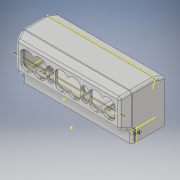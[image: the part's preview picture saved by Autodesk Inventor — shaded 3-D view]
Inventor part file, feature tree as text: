
AUTODESK INVENTOR PART (.ipt)
format: ipt  version: 2019 (Build 230136000, 136)  size: 1,148,416 bytes
history: native  units: mm
features: reference x93, sketch x32, extrude x29, plane x11, other x10, projected_geometry x10, mirror x6, hole x3, fillet x2, pattern_linear x1
ambient origin geometry x8: Origin, YZ Plane, XZ Plane, XY Plane, X Axis, Y Axis, Z Axis, Center Point
bodies: Body1 (feature_tree), Body2 (feature_tree), Body3 (feature_tree)
feature tree (197):
  other  "Querschnitt1"
  extrude  "Extrusion2"  Depth=4.0mm TaperAngle=0.0deg
  extrude  "Extrusion3"  TaperAngle=0.0deg  [1 undecoded]
  extrude  "Extrusion4"  Depth=4.0mm TaperAngle=0.0deg
  extrude  "Extrusion5"  Depth=4.0mm
  extrude  "Extrusion6"  Depth=0.5mm
  extrude  "Extrusion7"  Depth=0.5mm
  extrude  "Extrusion8"  Depth=4.0mm
  fillet  "Rundung1"  Radius=45.0mm
  extrude  "Extrusion9"  Depth=12.217305mm
  hole  "Bohrung1"  [1 undecoded]
  plane  "Arbeitsebene9"
  plane  "Arbeitsebene10"
  plane  "Arbeitsebene11"
  plane  "Arbeitsebene12"
  plane  "Arbeitsebene13"
  extrude  "Extrusion17"  Depth=30.0mm TaperAngle=0.0deg
  plane  "Arbeitsebene14"
  plane  "Arbeitsebene15"
  mirror  "Spiegeln4"
  extrude  "Extrusion18"  Depth=30.0mm TaperAngle=0.0deg
  extrude  "Extrusion19"  Depth=100.0mm
  extrude  "Extrusion20"  TaperAngle=0.0deg  [1 undecoded]
  mirror  "Spiegeln5"
  mirror  "Spiegeln6"
  mirror  "Spiegeln7"
  extrude  "Extrusion21"  Depth=4.0mm
  extrude  "Extrusion22"  Depth=20.0mm TaperAngle=0.0deg
  sketch  "Skizze31"  dims[d84=39.0mm d85=0.0mm d87=4.0mm]
  extrude  "Extrusion23"  Depth=15.0mm
  extrude  "Extrusion24"  Depth=100.0mm TaperAngle=0.0deg
  plane  "Arbeitsebene16"
  plane  "Arbeitsebene17"
  sketch  "Skizze34"  dims[d88=20.0mm d89=0.0mm d90=20.0mm d91=0.0mm]
  plane  "Arbeitsebene19"
  extrude  "Extrusion27"  Depth=1.0mm TaperAngle=0.0deg
  extrude  "Extrusion28"  Depth=0.14mm
  extrude  "Extrusion29"  Depth=1.0mm
  hole  "Bohrung2"  [1 undecoded]
  pattern_linear  "Rechteckige Anordnung1"  Count1=3 Spacing1=57.0mm
  extrude  "Extrusion30"  Depth=4.0mm TaperAngle=0.0deg
  plane  "Arbeitsebene20"
  extrude  "Extrusion34"  Depth=10.0mm
  extrude  "Extrusion35"  Depth=10.0mm TaperAngle=0.0deg
  extrude  "Extrusion36"  Depth=10.0mm
  extrude  "Extrusion37"  Depth=2.5mm
  extrude  "Extrusion38"  Depth=1.0mm
  extrude  "Extrusion39"  Depth=4.0mm TaperAngle=0.0deg
  extrude  "Extrusion40"  Depth=4.0mm
  extrude  "Extrusion41"  Depth=4.0mm
  mirror  "Spiegeln8"
  hole  "Bohrung3"  [1 undecoded]
  extrude  "Extrusion42"  Depth=4.0mm
  mirror  "Spiegeln9"
  fillet  "Rundung2"  Radius=98.0mm
  sketch  "Skizze1"  dims[d3=4.0mm d4=0.0mm d5=4.0mm d6=0.0mm]
  reference  "Referenz1"
  reference  "Referenz2"
  reference  "Referenz3"
  reference  "Referenz4"
  reference  "Referenz5"
  reference  "Referenz6"
  reference  "Referenz7"
  reference  "Referenz8"
  sketch  "Skizze2"  dims[d7=4.0mm d8=0.0mm d9=0.0mm d10=0.0mm]
  reference  "Referenz9"
  reference  "Referenz10"
  reference  "Referenz11"
  reference  "Referenz12"
  reference  "Referenz13"
  reference  "Referenz14"
  reference  "Referenz15"
  reference  "Referenz16"
  reference  "Referenz17"
  reference  "Referenz18"
  reference  "Referenz19"
  reference  "Referenz20"
  sketch  "Skizze3"  dims[d11=4.0mm d12=0.0mm d13=4.0mm d14=0.0mm]
  reference  "Referenz21"
  reference  "Referenz22"
  reference  "Referenz23"
  reference  "Referenz24"
  reference  "Referenz25"
  reference  "Referenz26"
  reference  "Referenz27"
  reference  "Referenz28"
  reference  "Referenz29"
  reference  "Referenz30"
  reference  "Referenz31"
  reference  "Referenz32"
  sketch  "Skizze4"  dims[d15=4.0mm d16=0.0mm d17=1.5mm]
  reference  "Referenz33"
  reference  "Referenz34"
  reference  "Referenz35"
  reference  "Referenz36"
  reference  "Referenz37"
  reference  "Referenz38"
  reference  "Referenz39"
  reference  "Referenz40"
  reference  "Referenz41"
  reference  "Referenz42"
  reference  "Referenz43"
  reference  "Referenz44"
  reference  "Referenz45"
  reference  "Referenz46"
  reference  "Referenz47"
  reference  "Referenz48"
  reference  "Referenz49"
  reference  "Referenz50"
  reference  "Referenz51"
  reference  "Referenz52"
  reference  "Referenz53"
  reference  "Referenz54"
  reference  "Referenz55"
  reference  "Referenz56"
  sketch  "Skizze5"  dims[d18=170.0mm d19=0.5mm]
  reference  "Referenz57"
  reference  "Referenz58"
  reference  "Referenz59"
  reference  "Referenz60"
  reference  "Referenz61"
  reference  "Referenz62"
  reference  "Referenz63"
  reference  "Referenz64"
  reference  "Referenz65"
  reference  "Referenz66"
  reference  "Referenz67"
  reference  "Referenz68"
  sketch  "Skizze6"  dims[d20=0.5mm d21=0.5mm]
  reference  "Referenz69"
  reference  "Referenz70"
  reference  "Referenz71"
  reference  "Referenz72"
  reference  "Referenz73"
  reference  "Referenz74"
  reference  "Referenz75"
  reference  "Referenz76"
  reference  "Referenz77"
  reference  "Referenz78"
  reference  "Referenz79"
  reference  "Referenz80"
  sketch  "Skizze7"  dims[d22=4.0mm d23=0.0mm d24=13.0mm]
  reference  "Referenz81"
  reference  "Referenz82"
  reference  "Referenz83"
  reference  "Referenz84"
  reference  "Referenz85"
  reference  "Referenz86"
  reference  "Referenz87"
  reference  "Referenz88"
  reference  "Referenz89"
  reference  "Referenz90"
  reference  "Referenz91"
  reference  "Referenz92"
  sketch  "Skizze8"  dims[d25=11.5mm d26=6.0mm d27=7.5mm d28=2.0mm d29=90.0deg d30=10.65mm d31=20.594885mm]
  projected_geometry  "Projizierte Kontur1"
  sketch  "Skizze9"  dims[d42=0.5mm d43=2.0mm d44=0.0mm d45=20.0mm d61=45.0mm]
  sketch  "Skizze24"  dims[d63=12.217305mm d64=12.217305mm]
  sketch  "Skizze26"  dims[d65=12.217305mm d66=90.0deg d69=90.0deg d70=4.0mm]
  sketch  "Skizze27"  dims[d71=30.0mm d72=0.0mm d73=30.0mm d74=0.0mm]
  projected_geometry  "Projizierte Kontur3"
  sketch  "Skizze28"  dims[d75=30.0mm d76=0.0mm d77=30.0mm d78=0.0mm]
  projected_geometry  "Projizierte Kontur4"
  sketch  "Skizze29"  dims[d79=15.0mm d80=100.0mm]
  sketch  "Skizze30"  dims[d81=100.0mm d82=0.0mm d83=0.0mm]
  projected_geometry  "Projizierte Kontur5"
  projected_geometry  "Projizierte Kontur6"
  projected_geometry  "Projizierte Kontur7"
  sketch  "Skizze36"  dims[d92=12.217305mm d98=15.0mm]
  sketch  "Skizze37"  dims[d99=100.0mm d100=0.0mm d101=100.0mm d102=0.0mm]
  sketch  "Skizze38"  dims[d103=1.0mm d104=12.0mm d105=12.0mm d106=0.0mm d107=0.0mm]
  reference  "Referenz98"
  sketch  "Skizze39"  dims[d108=2.0mm d109=0.14mm]
  sketch  "Skizze41"  dims[d110=1.65mm d111=1.0mm]
  projected_geometry  "Projizierte Kontur11"
  sketch  "Skizze45"  dims[d112=1.0mm d113=2.0mm]
  sketch  "Skizze46"  dims[d114=16.0mm]
  sketch  "Skizze47"  dims[d115=1.5mm]
  sketch  "Skizze48"  dims[d116=1.5mm d117=6.0mm d118=4.0mm d119=2.0mm d120=90.0deg d121=5.0mm d122=20.594885mm d123=30.0mm d125=57.0mm]
  sketch  "Skizze49"  dims[d126=10.0mm d128=10.0mm d129=4.0mm d130=0.0mm]
  sketch  "Skizze50"  dims[d134=-1.0mm d146=10.0mm]
  sketch  "Skizze51"  dims[d147=10.0mm d148=46.0mm d149=0.0mm]
  projected_geometry  "Projizierte Kontur13"
  sketch  "Skizze52"  dims[d150=10.0mm d151=10.0mm]
  sketch  "Skizze53"  dims[d152=46.0mm d153=0.0mm d154=2.5mm]
  projected_geometry  "Projizierte Kontur14"
  sketch  "Skizze54"  dims[d155=2.0mm d156=1.0mm d157=47.0mm d158=0.0mm d162=7.0mm d163=2.5mm d164=6.0mm d165=4.0mm d166=98.0mm d167=46.0mm d168=0.0mm d169=2.0mm d171=99.2mm d172=47.0mm d173=0.0mm d174=51.7mm d175=2.0mm d176=1.0mm d177=47.0mm d178=0.0mm d179=47.0mm d180=0.0mm d181=0.872665mm d182=3.0mm d183=4.0mm d184=47.0mm d185=0.0mm d186=3.5mm d187=6.0mm d188=4.0mm d189=2.0mm d190=90.0deg d191=15.0mm d192=20.594885mm d193=5.8mm d194=2.8mm d195=5.0mm d196=8.5mm d197=0.0mm d198=4.0mm]
  projected_geometry  "Projizierte Kontur15"
  parser-record x1  (decoder bookkeeping rows leaked as tree rows — omitted from the tree; the rows remain in map.json)
  other  "Zusammenbau.iam"
  other  "IN-12a:1"
  other  "IN-12a:2"
  other  "IN-12a:3"
  other  "IN-12a:4"
  other  "IN-12a:5"
  other  "IN-12a:6"
  other  "NixieModule_IN12.brd:2"
note: 5 required parameter values undecoded (feature->parameter linkage not recoverable at this tier; creation-order binding heuristic only, values carry confidence <= 0.55)
note: 1 file-system path scrubbed to <path> (originals preserved in map.json)
